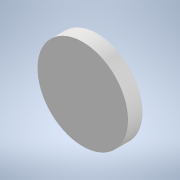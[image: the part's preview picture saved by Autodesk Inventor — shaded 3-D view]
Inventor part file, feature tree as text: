
AUTODESK INVENTOR PART (.ipt)
format: ipt  version: 2020 (Build 240168000, 168)  size: 99,840 bytes
history: native  units: mm
features: extrude x1, shell x1, sketch x1
ambient origin geometry x8: Origin, YZ Plane, XZ Plane, XY Plane, X Axis, Y Axis, Z Axis, Center Point
bodies: Solid1 (feature_tree)
feature tree (3):
  extrude  "Extrusion1"  Depth=40.0mm TaperAngle=0.0deg
  shell  "Shell1"  Thickness=4.0mm
  sketch  "Sketch1"  dims[d1=250.0mm d2=40.0mm d3=0.0mm d4=4.0mm]
